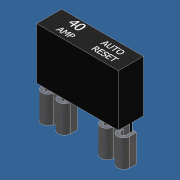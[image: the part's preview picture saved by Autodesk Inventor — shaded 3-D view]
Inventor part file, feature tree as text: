
AUTODESK INVENTOR PART (.ipt)
format: ipt  version: 2012 (Build 160160000, 160)  size: 364,032 bytes
history: native  units: mm (DEFAULTED — no unit token found)
features: extrude x4, sketch x4, plane x3, mirror x1, projected_geometry x1
ambient origin geometry x5: Origin, X Axis, Y Axis, Z Axis, Center Point
bodies: Solid1 (feature_tree)
feature tree (13):
  extrude  "Extrusion1"  Depth=8.89mm
  extrude  "Extrusion2"  Depth=0.8128mm
  extrude  "Extrusion3"  Depth=12.446mm TaperAngle=0.0deg
  mirror  "Mirror1"
  extrude  "Extrusion4"  Depth=10.16mm
  plane  "YZ Plane (RIGHT)"
  plane  "XZ Plane (TOP)"
  plane  "XY Plane (FRONT)"
  sketch  "Sketch2"  dims[d0=28.956mm d1=8.89mm]
  sketch  "Sketch3"  dims[d2=18.288mm d3=0.0mm d4=0.8128mm]
  sketch  "Sketch4"  dims[d5=8.001mm d6=12.446mm d7=0.0mm]
  projected_geometry  "Projected Loop1"
  sketch  "Sketch5"  dims[d8=0.5588mm d9=10.16mm d10=4.6482mm d11=1.524mm d12=9.652mm d13=0.0mm d14=0.00254mm d15=0.0mm]
